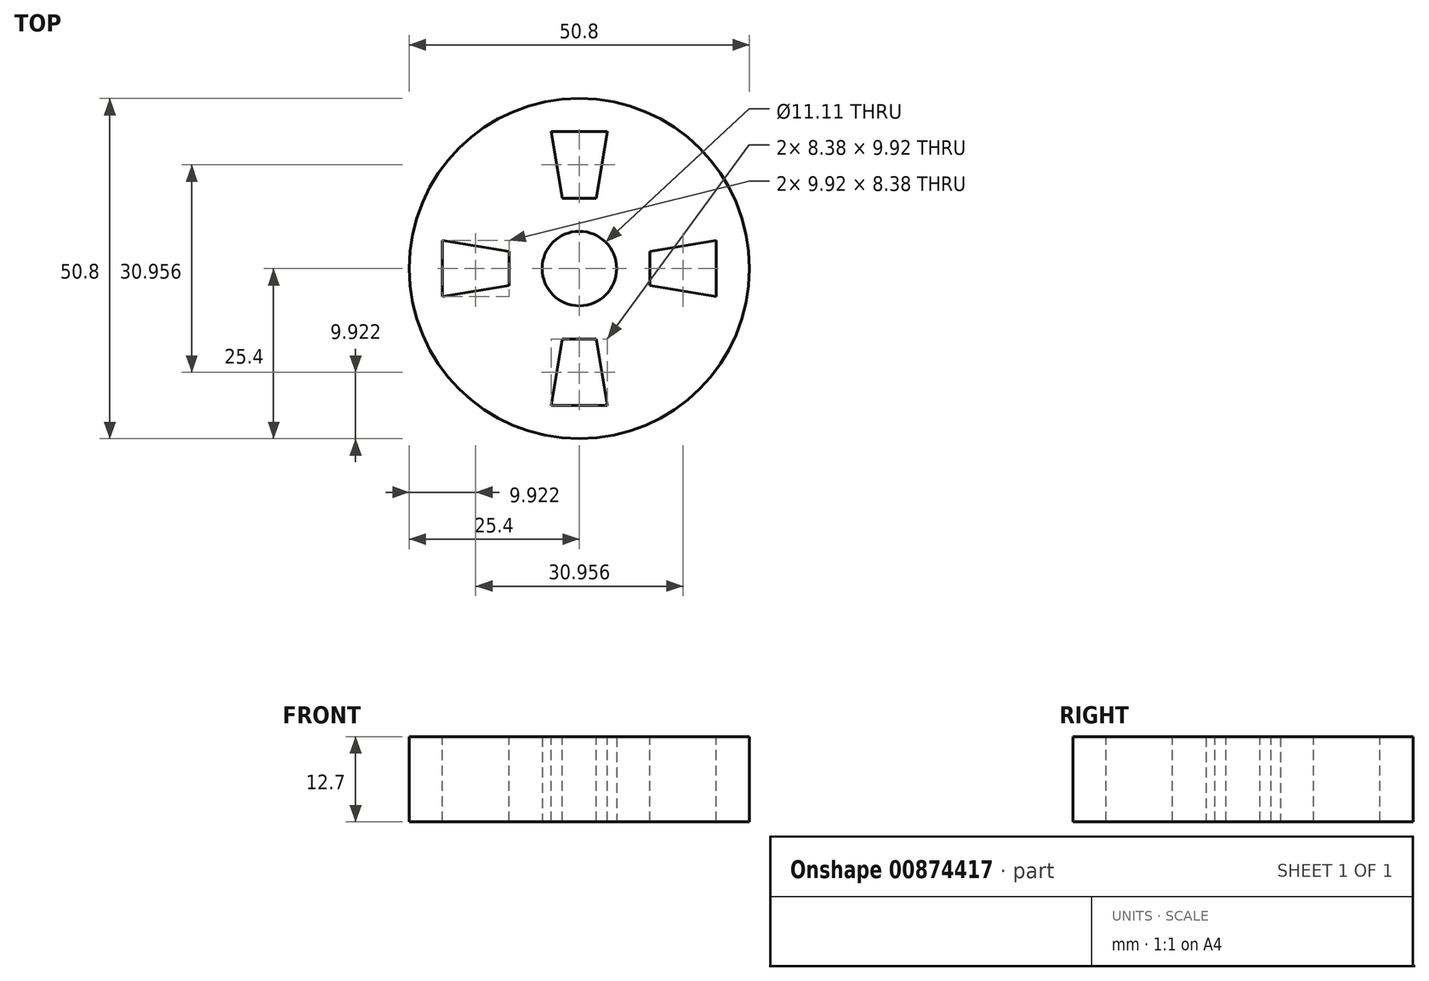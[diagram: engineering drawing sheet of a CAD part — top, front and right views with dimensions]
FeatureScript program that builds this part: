
annotation { "Feature Type Name" : "Feature", "Feature Type Description" : "" }
export const myFeature = defineFeature(function(context is Context, id is Id, definition is map)
    precondition{}
    {
        {
            var Q0;
            Q0=qCreatedBy(makeId("Top.planeOp"),FACE);
            var sketch = newSketch(context, id + "F0", { "sketchPlane" : qUnion([Q0])});
            skCircle(sketch, "E0", {"center": v(0, 0) * mm, "radius": 25.4 * mm});
            skCircle(sketch, "E1", {"center": v(0, 0) * mm, "radius": 5.56 * mm});
            skSolve(sketch);
        }
        {
            var Q0;
            Q0=makeQuery(id+"F0.imprint","IMPRINT",FACE,{"disambiguationData":[TD([[makeQuery(id+"F0.imprint","IMPRINT",EDGE,{"derivedFrom":sQuery(id+"F0.wireOp",EDGE,"E0")}),1.0]])]});
            extrude(context, id + "F1", {"entities" : qUnion([Q0]), "depth" : 12.7 * mm, "offsetDistance" : 25.4 * mm});
        }
        {
            var Q0;
            Q0=makeQuery(id+"F1.opExtrude","CAP_FACE",FACE,{"disambiguationData":[OSD([sQuery(id+"F0.wireOp",EDGE,"E0"),sQuery(id+"F0.wireOp",EDGE,"E1")])],"isStart":false});
            var sketch = newSketch(context, id + "F2", { "sketchPlane" : qUnion([Q0])});
            skLineSegment(sketch, "E2", {"start": v(0, 5.56) * mm, "end": v(0, 10.52) * mm, "construction": true});
            skLineSegment(sketch, "E3", {"start": v(0, 15.48) * mm, "end": v(0, 20.44) * mm, "construction": true});
            skLineSegment(sketch, "E4", {"start": v(0, 20.44) * mm, "end": v(0, 25.4) * mm, "construction": true});
            skLineSegment(sketch, "E5", {"start": v(0, 10.52) * mm, "end": v(0, 15.48) * mm, "construction": true});
            skLineSegment(sketch, "E6", {"start": v(-4.2, 20.44) * mm, "end": v(4.2, 20.44) * mm});
            skLineSegment(sketch, "E7", {"start": v(2.54, 10.52) * mm, "end": v(-2.54, 10.52) * mm});
            skLineSegment(sketch, "E8", {"start": v(-4.2, 20.44) * mm, "end": v(-2.54, 10.52) * mm});
            skLineSegment(sketch, "E9", {"start": v(4.2, 20.44) * mm, "end": v(2.54, 10.52) * mm});
            skLineSegment(sketch, "E10", {"start": v(-5.56, 0) * mm, "end": v(-10.52, 0) * mm, "construction": true});
            skLineSegment(sketch, "E11", {"start": v(0, -5.56) * mm, "end": v(0, -10.52) * mm, "construction": true});
            skLineSegment(sketch, "E12", {"start": v(5.56, 0) * mm, "end": v(10.52, 0) * mm, "construction": true});
            skLineSegment(sketch, "E13", {"start": v(15.48, 0) * mm, "end": v(20.44, 0) * mm, "construction": true});
            skLineSegment(sketch, "E14", {"start": v(20.44, 0) * mm, "end": v(25.4, 0) * mm, "construction": true});
            skLineSegment(sketch, "E15", {"start": v(10.52, 0) * mm, "end": v(15.48, 0) * mm, "construction": true});
            skLineSegment(sketch, "E16", {"start": v(-15.48, 0) * mm, "end": v(-20.44, 0) * mm, "construction": true});
            skLineSegment(sketch, "E17", {"start": v(-10.52, 0) * mm, "end": v(-15.48, 0) * mm, "construction": true});
            skLineSegment(sketch, "E18", {"start": v(-20.44, 0) * mm, "end": v(-25.4, 0) * mm, "construction": true});
            skLineSegment(sketch, "E19", {"start": v(0, -15.48) * mm, "end": v(0, -20.44) * mm, "construction": true});
            skLineSegment(sketch, "E20", {"start": v(0, -10.52) * mm, "end": v(0, -15.48) * mm, "construction": true});
            skLineSegment(sketch, "E21", {"start": v(0, -20.44) * mm, "end": v(0, -25.4) * mm, "construction": true});
            skLineSegment(sketch, "E22", {"start": v(20.44, 4.2) * mm, "end": v(20.44, -4.2) * mm});
            skLineSegment(sketch, "E23", {"start": v(10.52, 2.54) * mm, "end": v(10.52, -2.54) * mm});
            skLineSegment(sketch, "E24", {"start": v(10.52, 2.54) * mm, "end": v(20.44, 4.2) * mm});
            skLineSegment(sketch, "E25", {"start": v(20.44, -4.2) * mm, "end": v(10.52, -2.54) * mm});
            skPoint(sketch, "E26.endSnap0", {"position": v(0, -17.96) * mm});
            skLineSegment(sketch, "E27", {"start": v(4.2, -20.44) * mm, "end": v(-4.2, -20.44) * mm});
            skLineSegment(sketch, "E28", {"start": v(2.54, -10.52) * mm, "end": v(-2.54, -10.52) * mm});
            skLineSegment(sketch, "E29", {"start": v(-2.54, -10.52) * mm, "end": v(-4.2, -20.44) * mm});
            skLineSegment(sketch, "E30", {"start": v(2.54, -10.52) * mm, "end": v(4.2, -20.44) * mm});
            skLineSegment(sketch, "E31", {"start": v(-20.44, 4.2) * mm, "end": v(-20.44, -4.2) * mm});
            skLineSegment(sketch, "E32", {"start": v(-10.52, 2.54) * mm, "end": v(-10.52, -2.54) * mm});
            skLineSegment(sketch, "E33", {"start": v(-20.44, 4.2) * mm, "end": v(-10.52, 2.54) * mm});
            skLineSegment(sketch, "E34", {"start": v(-10.52, -2.54) * mm, "end": v(-20.44, -4.2) * mm});
            skSolve(sketch);
        }
        {
            var Q0;
            Q0=makeQuery(id+"F2.imprint","IMPRINT",FACE,{"disambiguationData":[TD([[makeQuery(id+"F2.imprint","IMPRINT",EDGE,{"derivedFrom":sQuery(id+"F2.wireOp",EDGE,"E6")}),-1.0]])]});
            var Q1;
            Q1=makeQuery(id+"F2.imprint","IMPRINT",FACE,{"disambiguationData":[TD([[makeQuery(id+"F2.imprint","IMPRINT",EDGE,{"derivedFrom":sQuery(id+"F2.wireOp",EDGE,"E31")}),1.0]])]});
            var Q2;
            Q2=makeQuery(id+"F2.imprint","IMPRINT",FACE,{"disambiguationData":[TD([[makeQuery(id+"F2.imprint","IMPRINT",EDGE,{"derivedFrom":sQuery(id+"F2.wireOp",EDGE,"E22")}),-1.0]])]});
            var Q3;
            Q3=makeQuery(id+"F2.imprint","IMPRINT",FACE,{"disambiguationData":[TD([[makeQuery(id+"F2.imprint","IMPRINT",EDGE,{"derivedFrom":sQuery(id+"F2.wireOp",EDGE,"E27")}),-1.0]])]});
            extrude(context, id + "F3", {"entities" : qUnion([Q0, Q1, Q2, Q3]), "operationType" : NewBodyOperationType.REMOVE, "oppositeDirection" : true, "depth" : 25.4 * mm, "offsetDistance" : 25.4 * mm});
        }
    });
